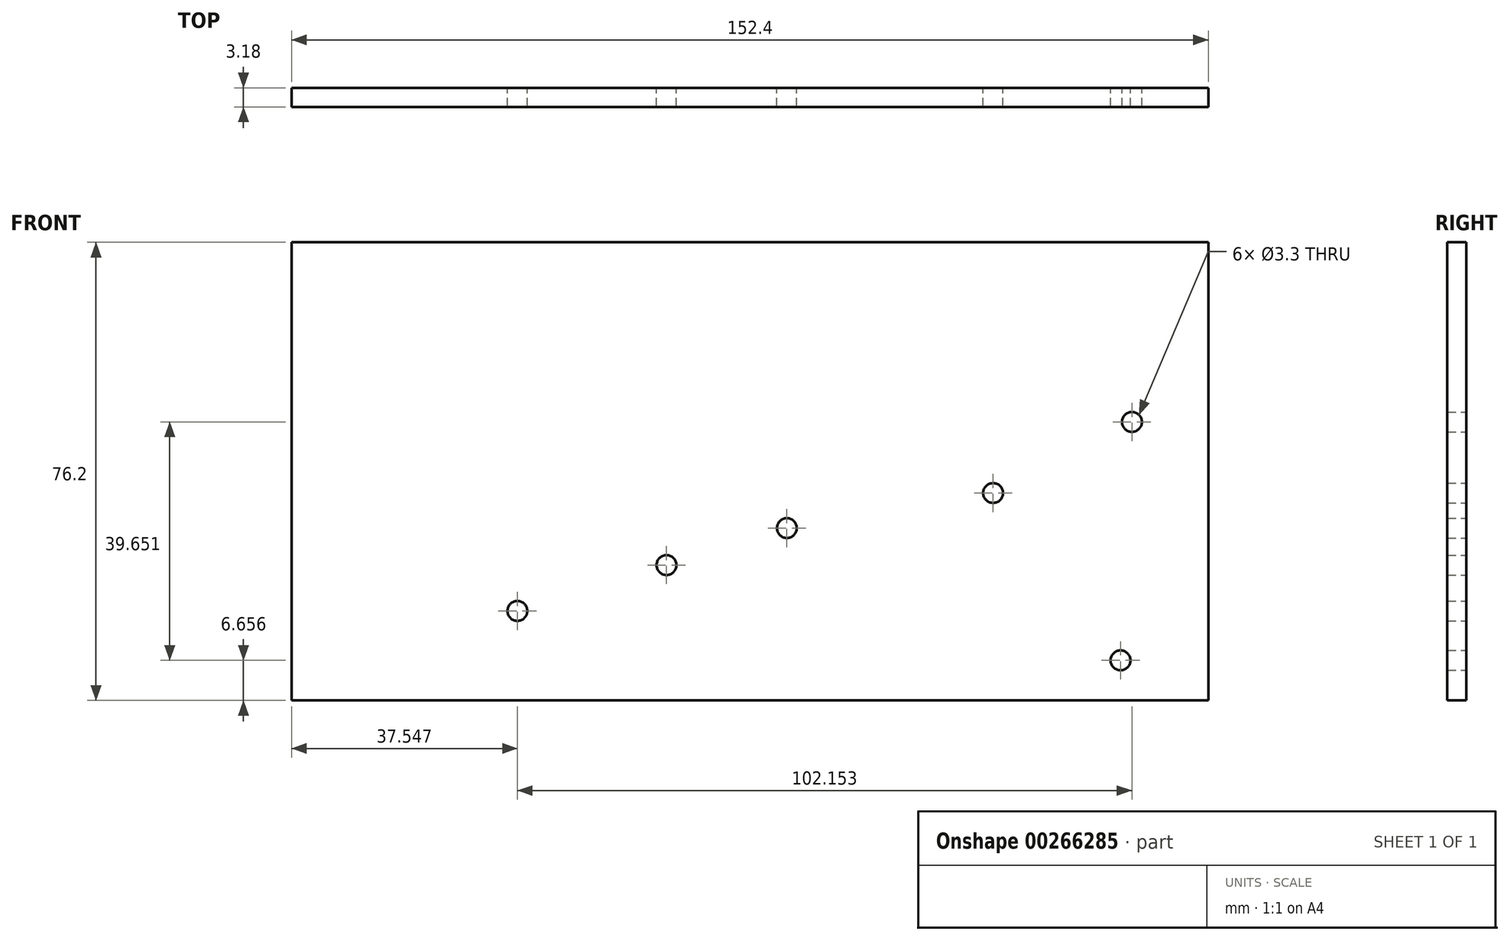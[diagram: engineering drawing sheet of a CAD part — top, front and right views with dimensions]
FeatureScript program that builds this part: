
annotation { "Feature Type Name" : "Feature", "Feature Type Description" : "" }
export const myFeature = defineFeature(function(context is Context, id is Id, definition is map)
    precondition{}
    {
        {
            var Q0;
            Q0=qCreatedBy(makeId("Front.planeOp"),FACE);
            var sketch = newSketch(context, id + "F0", { "sketchPlane" : qUnion([Q0])});
            skLineSegment(sketch, "E0.bottom", {"start": v(0, 0) * mm, "end": v(-152.4, 0) * mm});
            skLineSegment(sketch, "E0.top", {"start": v(0, 76.2) * mm, "end": v(-152.4, 76.2) * mm});
            skLineSegment(sketch, "E0.left", {"start": v(0, 0) * mm, "end": v(0, 76.2) * mm});
            skLineSegment(sketch, "E0.right", {"start": v(-152.4, 0) * mm, "end": v(-152.4, 76.2) * mm});
            skCircle(sketch, "E1", {"center": v(-12.7, 46.3) * mm, "radius": 1.65 * mm});
            skCircle(sketch, "E2", {"center": v(-35.78, 34.49) * mm, "radius": 1.65 * mm});
            skCircle(sketch, "E3", {"center": v(-70.06, 28.65) * mm, "radius": 1.65 * mm});
            skCircle(sketch, "E4", {"center": v(-90.07, 22.5) * mm, "radius": 1.65 * mm});
            skCircle(sketch, "E5", {"center": v(-114.85, 14.87) * mm, "radius": 1.65 * mm});
            skCircle(sketch, "E6", {"center": v(-14.6, 6.66) * mm, "radius": 1.65 * mm});
            skSolve(sketch);
        }
        {
            var Q0;
            Q0 = qSketchRegion(id + "F0", true);
            extrude(context, id + "F1", {"entities" : qUnion([Q0]), "depth" : 3.17 * mm});
        }
    });
